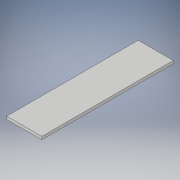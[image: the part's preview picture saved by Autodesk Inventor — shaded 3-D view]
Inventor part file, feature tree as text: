
AUTODESK INVENTOR PART (.ipt)
format: ipt  version: 2019 (Build 230136000, 136)  size: 91,136 bytes
history: native  units: mm
features: other x1, extrude x1, sketch x1
ambient origin geometry x8: Origin, YZ Plane, XZ Plane, XY Plane, X Axis, Y Axis, Z Axis, Center Point
bodies: Body1 (feature_tree)
feature tree (3):
  other  "Těleso1"
  extrude  "Vysunutí1"  Depth=450.0mm
  sketch  "Náčrt1"
